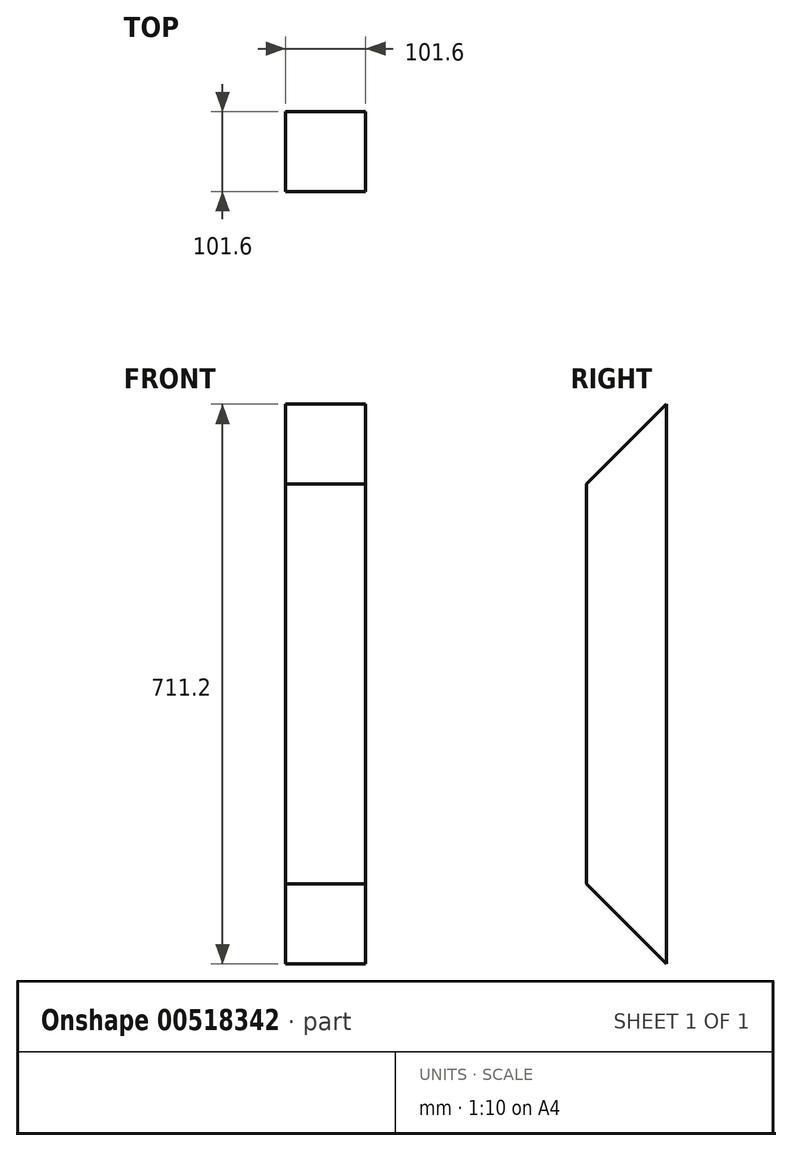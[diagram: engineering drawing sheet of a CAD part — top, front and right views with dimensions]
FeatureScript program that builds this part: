
annotation { "Feature Type Name" : "Feature", "Feature Type Description" : "" }
export const myFeature = defineFeature(function(context is Context, id is Id, definition is map)
    precondition{}
    {
        {
            var Q0;
            Q0=qCreatedBy(makeId("Right.planeOp"),FACE);
            var sketch = newSketch(context, id + "F0", { "sketchPlane" : qUnion([Q0])});
            skLineSegment(sketch, "E0.bottom", {"start": v(-50.8, 355.6) * mm, "end": v(50.8, 355.6) * mm});
            skLineSegment(sketch, "E0.top", {"start": v(-50.8, -355.6) * mm, "end": v(50.8, -355.6) * mm});
            skLineSegment(sketch, "E0.left", {"start": v(-50.8, 355.6) * mm, "end": v(-50.8, -355.6) * mm});
            skLineSegment(sketch, "E0.right", {"start": v(50.8, 355.6) * mm, "end": v(50.8, -355.6) * mm});
            skPoint(sketch, "E0.middle", {"position": v(0, 0) * mm});
            skSolve(sketch);
        }
        {
            var Q0;
            Q0=makeQuery(id+"F0.imprint","IMPRINT",FACE,{"disambiguationData":[TD([[makeQuery(id+"F0.imprint","IMPRINT",EDGE,{"derivedFrom":sQuery(id+"F0.wireOp",EDGE,"E0.bottom")}),-1.0]])]});
            extrude(context, id + "F1", {"entities" : qUnion([Q0]), "depth" : 101.6 * mm, "offsetDistance" : 25.4 * mm});
        }
        {
            var Q0;
            Q0=makeQuery(id+"F1.opExtrude","CAP_FACE",FACE,{"disambiguationData":[OSD([sQuery(id+"F0.wireOp",EDGE,"E0.bottom"),sQuery(id+"F0.wireOp",EDGE,"E0.top"),sQuery(id+"F0.wireOp",EDGE,"E0.left"),sQuery(id+"F0.wireOp",EDGE,"E0.right")])],"isStart":false});
            var sketch = newSketch(context, id + "F2", { "sketchPlane" : qUnion([Q0])});
            skLineSegment(sketch, "E1", {"start": v(50.8, 355.6) * mm, "end": v(-50.8, 254) * mm});
            skLineSegment(sketch, "E2", {"start": v(-50.8, 254) * mm, "end": v(-50.8, 355.6) * mm});
            skLineSegment(sketch, "E3", {"start": v(-50.8, 355.6) * mm, "end": v(50.8, 355.6) * mm});
            skLineSegment(sketch, "E4", {"start": v(50.8, -355.6) * mm, "end": v(-50.8, -254) * mm});
            skLineSegment(sketch, "E5", {"start": v(-50.8, -254) * mm, "end": v(-50.8, -355.6) * mm});
            skLineSegment(sketch, "E6", {"start": v(-50.8, -355.6) * mm, "end": v(50.8, -355.6) * mm});
            skSolve(sketch);
        }
        {
            var Q0;
            Q0 = qSketchRegion(id + "F2", true);
            extrude(context, id + "F3", {"entities" : qUnion([Q0]), "operationType" : NewBodyOperationType.REMOVE, "oppositeDirection" : true, "depth" : 101.6 * mm, "offsetDistance" : 25.4 * mm});
        }
    });
